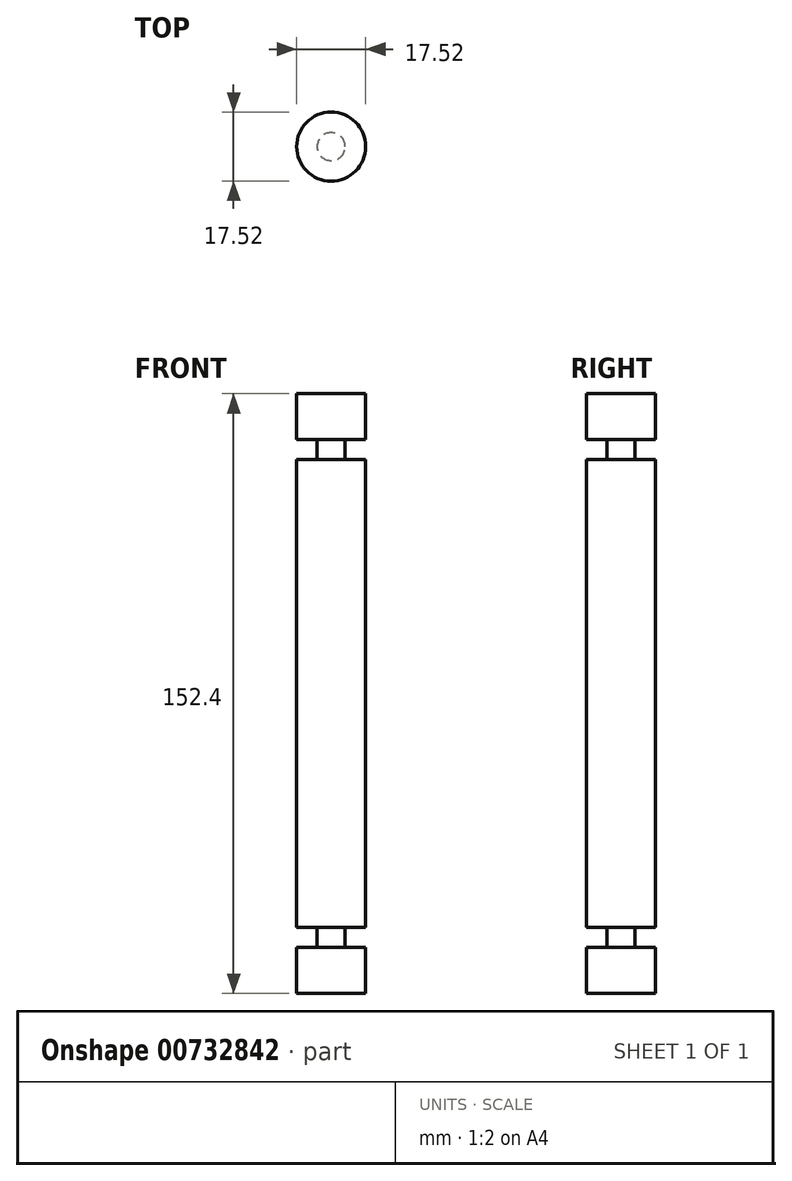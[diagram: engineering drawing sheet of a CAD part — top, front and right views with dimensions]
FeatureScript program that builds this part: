
annotation { "Feature Type Name" : "Feature", "Feature Type Description" : "" }
export const myFeature = defineFeature(function(context is Context, id is Id, definition is map)
    precondition{}
    {
        {
            var Q0;
            Q0=qCreatedBy(makeId("Top.planeOp"),FACE);
            var sketch = newSketch(context, id + "F0", { "sketchPlane" : qUnion([Q0])});
            skCircle(sketch, "E0", {"center": v(0, 0) * mm, "radius": 8.76 * mm});
            skSolve(sketch);
        }
        {
            var Q0;
            Q0=qSketchRegion(id+"F0",true);
            extrude(context, id + "F1", {"entities" : qUnion([Q0]), "depth" : 59.44 * mm, "offsetDistance" : 25.4 * mm, "hasSecondDirection" : true, "secondDirectionOppositeDirection" : true, "secondDirectionDepth" : 59.44 * mm});
        }
        {
            var Q0;
            Q0=qCreatedBy(makeId("Top.planeOp"),FACE);
            var sketch = newSketch(context, id + "F2", { "sketchPlane" : qUnion([Q0])});
            skCircle(sketch, "E1", {"center": v(0, 0) * mm, "radius": 3.56 * mm});
            skSolve(sketch);
        }
        {
            var Q0;
            Q0 = qSketchRegion(id + "F2", true);
            extrude(context, id + "F3", {"entities" : qUnion([Q0]), "operationType" : NewBodyOperationType.ADD, "depth" : 76.2 * mm, "offsetDistance" : 25.4 * mm, "hasSecondDirection" : true, "secondDirectionOppositeDirection" : true, "secondDirectionDepth" : 76.2 * mm});
        }
        {
            var Q0;
            Q0=qCreatedBy(makeId("Top.planeOp"),FACE);
            cPlane(context, id + "F4", {"entities" : qUnion([Q0]), "cplaneType" : CPlaneType.OFFSET, "offset" : 76.2 * mm, "width" : 152.4 * mm, "height" : 152.4 * mm});
        }
        {
            var Q0;
            Q0=qCreatedBy(makeId("Top.planeOp"),FACE);
            cPlane(context, id + "F5", {"entities" : qUnion([Q0]), "cplaneType" : CPlaneType.OFFSET, "offset" : 76.2 * mm, "oppositeDirection" : true, "width" : 152.4 * mm, "height" : 152.4 * mm});
        }
        {
            var Q0;
            Q0=qCreatedBy(id+"F4.planeOp",FACE);
            var sketch = newSketch(context, id + "F6", { "sketchPlane" : qUnion([Q0])});
            skCircle(sketch, "E2", {"center": v(0, 0) * mm, "radius": 8.76 * mm});
            skSolve(sketch);
        }
        {
            var Q0;
            Q0 = qSketchRegion(id + "F6", true);
            extrude(context, id + "F7", {"entities" : qUnion([Q0]), "operationType" : NewBodyOperationType.ADD, "oppositeDirection" : true, "depth" : 11.68 * mm, "offsetDistance" : 25.4 * mm});
        }
        {
            var Q0;
            Q0=qCreatedBy(id+"F5.planeOp",FACE);
            var sketch = newSketch(context, id + "F8", { "sketchPlane" : qUnion([Q0])});
            skCircle(sketch, "E3", {"center": v(0, 0) * mm, "radius": 8.76 * mm});
            skSolve(sketch);
        }
        {
            var Q0;
            Q0 = qSketchRegion(id + "F8", true);
            extrude(context, id + "F9", {"entities" : qUnion([Q0]), "operationType" : NewBodyOperationType.ADD, "depth" : 11.68 * mm, "offsetDistance" : 25.4 * mm});
        }
    });
